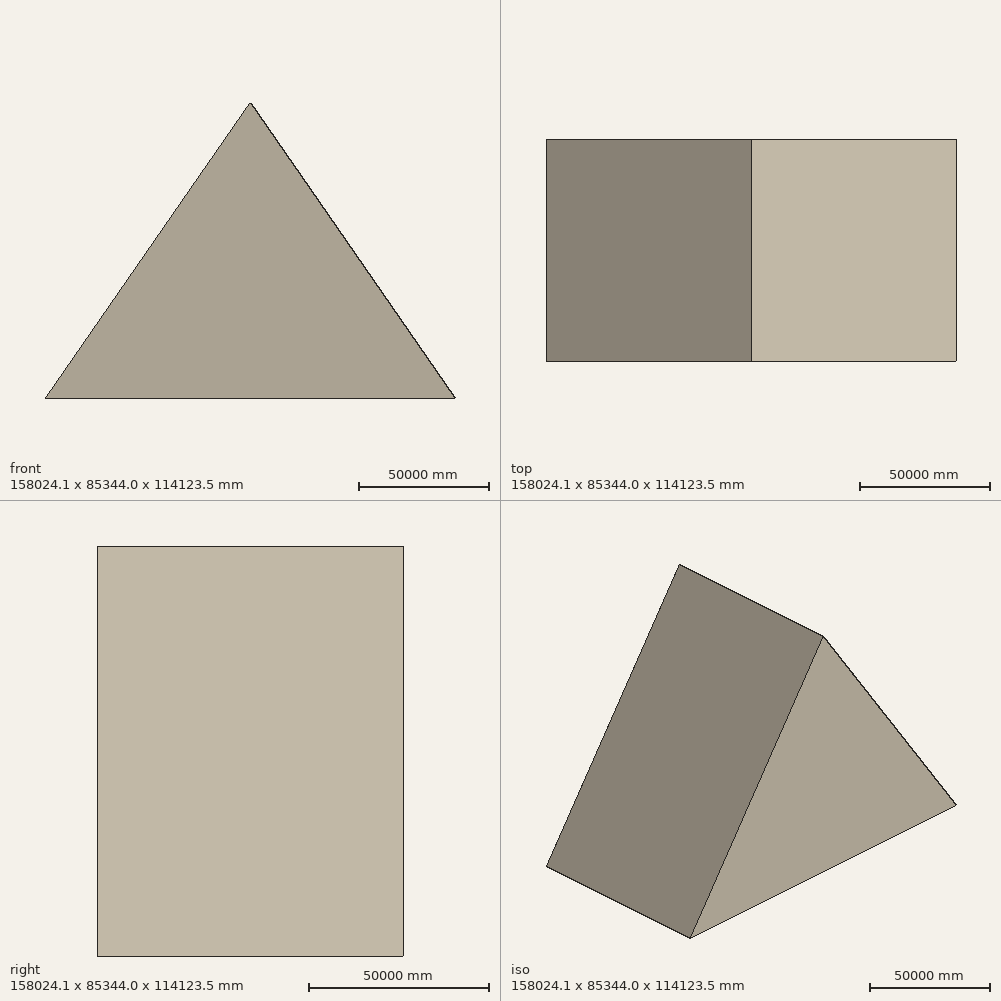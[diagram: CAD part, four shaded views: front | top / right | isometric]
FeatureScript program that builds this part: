
annotation { "Feature Type Name" : "Feature", "Feature Type Description" : "" }
export const myFeature = defineFeature(function(context is Context, id is Id, definition is map)
    precondition{}
    {
        {
            var Q0;
            Q0=qCreatedBy(makeId("Front.planeOp"),FACE);
            var sketch = newSketch(context, id + "F0", { "sketchPlane" : qUnion([Q0])});
            skLineSegment(sketch, "E0", {"start": v(0, 0) * mm, "end": v(79012.07, 114123.52) * mm});
            skLineSegment(sketch, "E1", {"start": v(79012.07, 114123.52) * mm, "end": v(158024.13, 0) * mm});
            skLineSegment(sketch, "E2", {"start": v(0, 0) * mm, "end": v(158024.13, 0) * mm});
            skSolve(sketch);
        }
        {
            var Q0;
            Q0=makeQuery(id+"F0.imprint","IMPRINT",FACE,{"disambiguationData":[TD([[makeQuery(id+"F0.imprint","IMPRINT",EDGE,{"derivedFrom":sQuery(id+"F0.wireOp",EDGE,"tT529lPS-NLeS-jIs2-LHs0-jXGKDi1karMX")}),-1.0]])]});
            var Q1;
            Q1=makeQuery(id+"F0.imprint","IMPRINT",FACE,{"disambiguationData":[TD([[makeQuery(id+"F0.imprint","IMPRINT",EDGE,{"derivedFrom":sQuery(id+"F0.wireOp",EDGE,"E0")}),-1.0]])]});
            extrude(context, id + "F1", {"entities" : qUnion([Q0, Q1]), "depth" : 85344 * mm, "offsetDistance" : 25.4 * mm});
        }
    });
